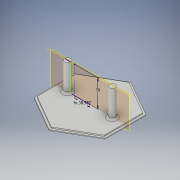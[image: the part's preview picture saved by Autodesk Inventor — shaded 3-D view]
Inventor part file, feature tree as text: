
AUTODESK INVENTOR PART (.ipt)
format: ipt  version: 2019.3 (Build 233278000, 278)  size: 166,912 bytes
history: native  units: mm
features: sketch x5, extrude x5, other x1, sweep x1, plane x1, fillet x1, mirror x1
ambient origin geometry x8: Origin, YZ Plane, XZ Plane, XY Plane, X Axis, Y Axis, Z Axis, Center Point
bodies: Solid1 (feature_tree)
feature tree (15):
  sketch  "Sketch2"  dims[d1=38.9815mm d14=210.0mm]
  sketch  "Sketch3"  dims[d15=5.0mm d16=5.0mm d17=0.0mm]
  extrude  "Extrusion3"  Depth=210.0mm
  extrude  "Extrusion4"  Depth=5.0mm TaperAngle=0.0deg
  other  "Work Axis3"
  sweep  "Sweep1"
  plane  "Work Plane1"
  sketch  "Sketch8"  dims[d38=11.0mm d39=4.0mm d40=60.0mm d42=34.557519mm]
  sketch  "Sketch10"  dims[d44=10.0mm d45=0.0mm d47=10.0mm d48=0.0mm d49=25.0mm d50=10.0mm d51=0.0mm d52=5.0mm d53=70.0mm]
  extrude  "Extrusion9"  Depth=4.0mm
  fillet  "Fillet5"  Radius=60.0mm
  mirror  "Mirror4"
  extrude  "Extrusion7"  Depth=10.0mm TaperAngle=0.0deg
  extrude  "Extrusion8"  Depth=70.0mm
  sketch  "Sketch7"  dims[d18=2.0mm d19=0.0mm d33=0.0mm d34=0.0mm]
